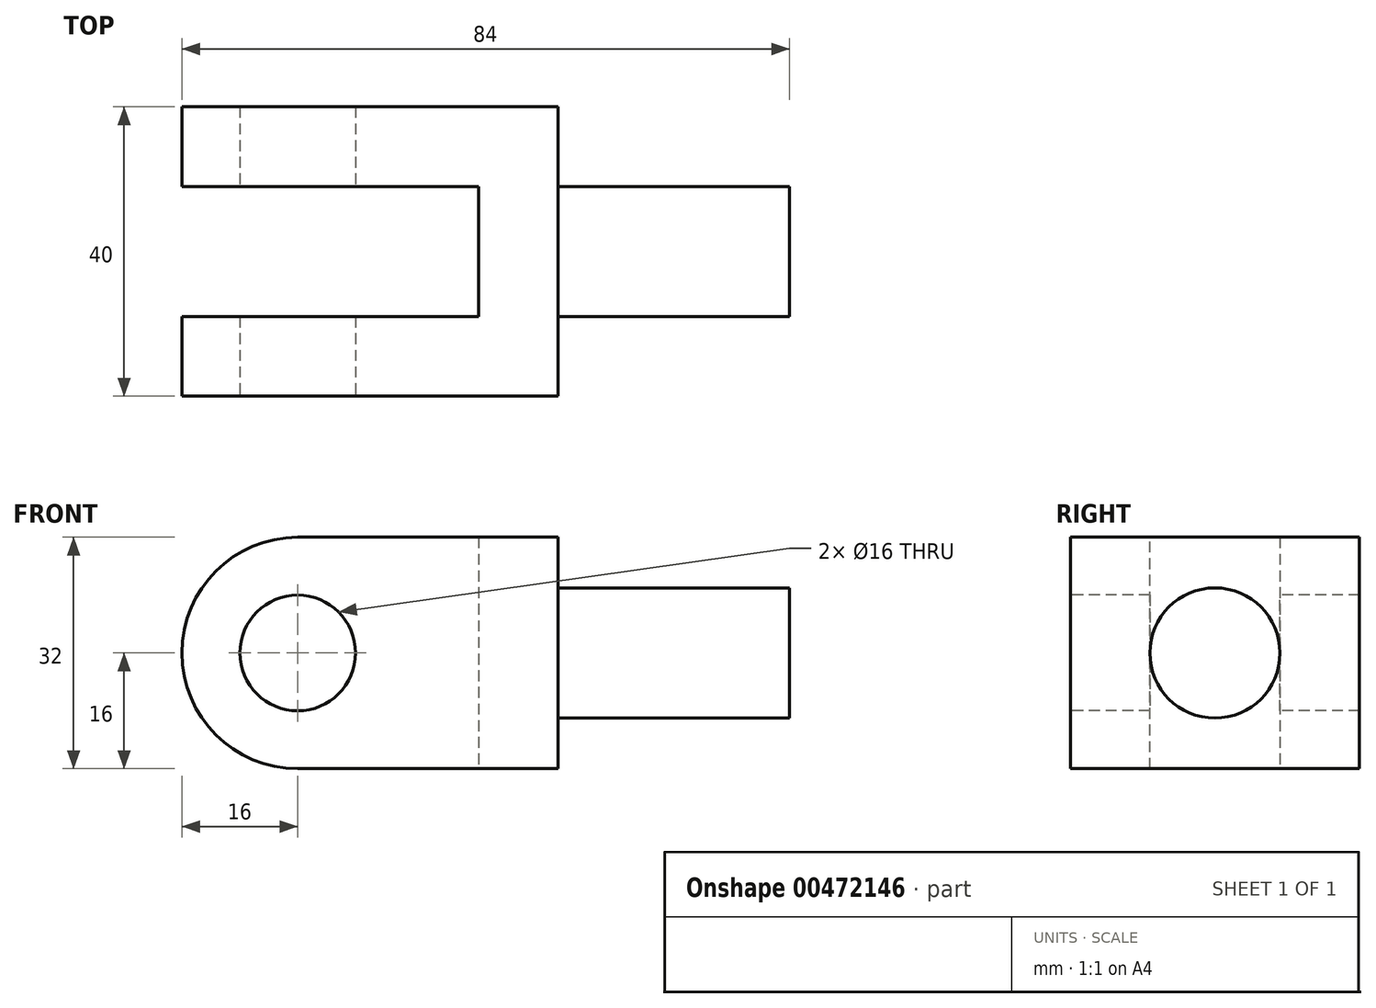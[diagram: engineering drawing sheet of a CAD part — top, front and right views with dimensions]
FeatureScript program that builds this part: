
annotation { "Feature Type Name" : "Feature", "Feature Type Description" : "" }
export const myFeature = defineFeature(function(context is Context, id is Id, definition is map)
    precondition{}
    {
        {
            var Q0;
            Q0=qCreatedBy(makeId("Top.planeOp"),FACE);
            var sketch = newSketch(context, id + "F0", { "sketchPlane" : qUnion([Q0])});
            skLineSegment(sketch, "E0.bottom", {"start": v(26, 20) * mm, "end": v(-26, 20) * mm});
            skLineSegment(sketch, "E0.top", {"start": v(26, -20) * mm, "end": v(-26, -20) * mm});
            skLineSegment(sketch, "E0.left", {"start": v(26, 20) * mm, "end": v(26, -20) * mm});
            skLineSegment(sketch, "E0.right", {"start": v(-26, 20) * mm, "end": v(-26, 9) * mm});
            skPoint(sketch, "E0.middle", {"position": v(0, 0) * mm});
            skLineSegment(sketch, "E1", {"start": v(-26, -20) * mm, "end": v(-26, -9) * mm});
            skLineSegment(sketch, "E2", {"start": v(-26, -9) * mm, "end": v(15, -9) * mm});
            skLineSegment(sketch, "E3", {"start": v(15, -9) * mm, "end": v(15, 9) * mm});
            skLineSegment(sketch, "E4", {"start": v(15, 9) * mm, "end": v(-26, 9) * mm});
            skLineSegment(sketch, "E5.trimOffspring", {"start": v(-26, -9) * mm, "end": v(-26, -20) * mm});
            skLineSegment(sketch, "E6", {"start": v(26, 9) * mm, "end": v(58, 9) * mm});
            skLineSegment(sketch, "E7", {"start": v(58, 9) * mm, "end": v(58, 0) * mm});
            skLineSegment(sketch, "E8", {"start": v(58, 0) * mm, "end": v(58, -9) * mm});
            skLineSegment(sketch, "E9", {"start": v(58, -9) * mm, "end": v(26, -9) * mm});
            skSolve(sketch);
        }
        {
            var Q0;
            {var subQ3=sQuery(id+"F0.wireOp",EDGE,"E0.bottom");Q0=makeQuery(id+"F0.imprint","IMPRINT",FACE,{"disambiguationData":[TD([[makeQuery(id+"F0.imprint","IMPRINT",EDGE,{"derivedFrom":subQ3}),1.0]])]});}
            extrude(context, id + "F1", {"entities" : qUnion([Q0]), "depth" : (16 * 2) * mm});
        }
        {
            var Q0;
            Q0=makeQuery(id+"F1.opExtrude","SWEPT_FACE",FACE,{"disambiguationData":[OSD([sQuery(id+"F0.wireOp",EDGE,"E0.top")])]});
            var sketch = newSketch(context, id + "F2", { "sketchPlane" : qUnion([Q0])});
            skLineSegment(sketch, "E10", {"start": v(26, 16) * mm, "end": v(-10, 16) * mm});
            skCircle(sketch, "E11", {"center": v(-10, 16) * mm, "radius": 8 * mm});
            skCircle(sketch, "E12", {"center": v(-10, 16) * mm, "radius": 16 * mm});
            skSolve(sketch);
        }
        {
            var Q0;
            {var subQ0=sQuery(id+"F2.wireOp",EDGE,"E12");var subQ1=sQuery(id+"F0.wireOp",EDGE,"E0.top");var subQ2=makeQuery(id+"F1.opExtrude","CAP_EDGE",EDGE,{"disambiguationData":[OSD([subQ1])],"isStart":false});var subQ3=makeQuery(id+"F2.imprint","INTERSECT",VERTEX,{"derivedFrom":[subQ2,subQ0]});Q0=makeQuery(id+"F2.imprint","IMPRINT",FACE,{"disambiguationData":[TD([[makeQuery(id+"F2.imprint","IMPRINT",EDGE,{"disambiguationData":[TD([[subQ3,-1.0]])],"derivedFrom":subQ0}),-1.0]])]});}
            var Q1;
            {var subQ0=sQuery(id+"F2.wireOp",EDGE,"E12");var subQ1=sQuery(id+"F0.wireOp",EDGE,"E0.top");var subQ4=makeQuery(id+"F1.opExtrude","CAP_EDGE",EDGE,{"disambiguationData":[OSD([subQ1])],"isStart":true});var subQ5=makeQuery(id+"F2.imprint","INTERSECT",VERTEX,{"derivedFrom":[subQ4,subQ0]});Q1=makeQuery(id+"F2.imprint","IMPRINT",FACE,{"disambiguationData":[TD([[makeQuery(id+"F2.imprint","IMPRINT",EDGE,{"disambiguationData":[TD([[subQ5,1.0]])],"derivedFrom":subQ0}),-1.0]])]});}
            var Q2;
            Q2=makeQuery(id+"F2.imprint","IMPRINT",FACE,{"disambiguationData":[TD([[makeQuery(id+"F2.imprint","IMPRINT",EDGE,{"derivedFrom":sQuery(id+"F2.wireOp",EDGE,"E11")}),1.0]])]});
            extrude(context, id + "F3", {"entities" : qUnion([Q0, Q1, Q2]), "operationType" : NewBodyOperationType.REMOVE, "oppositeDirection" : true, "depth" : 99.3 * mm});
        }
        {
            var Q0;
            Q0=makeQuery(id+"F1.opExtrude","SWEPT_FACE",FACE,{"disambiguationData":[OSD([sQuery(id+"F0.wireOp",EDGE,"E0.left")])]});
            var sketch = newSketch(context, id + "F4", { "sketchPlane" : qUnion([Q0])});
            skLineSegment(sketch, "E13", {"start": v(0, 32) * mm, "end": v(0, 0) * mm});
            skLineSegment(sketch, "E14", {"start": v(-20, 16) * mm, "end": v(20, 16) * mm});
            skCircle(sketch, "E15", {"center": v(0, 16) * mm, "radius": 9 * mm});
            skSolve(sketch);
        }
        {
            var Q0;
            Q0 = qSketchRegion(id + "F4", true);
            extrude(context, id + "F5", {"entities" : qUnion([Q0]), "operationType" : NewBodyOperationType.ADD, "depth" : 32 * mm});
        }
    });
